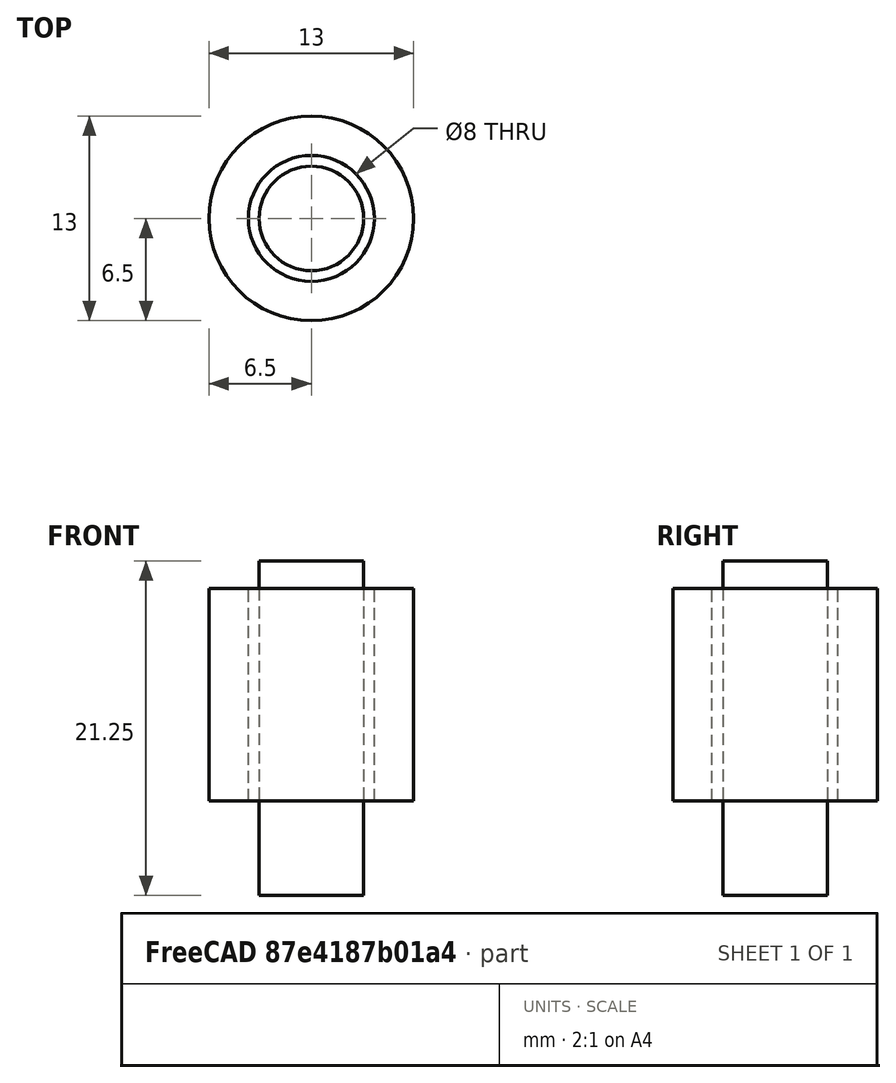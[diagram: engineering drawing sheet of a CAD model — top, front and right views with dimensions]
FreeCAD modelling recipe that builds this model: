
FCSTD DOCUMENT  (FreeCAD 0.18.4R)
Label: shower_handler_vtulka
License: FreeArt
LicenseURL: http://artlibre.org/licence/lal
objects: Part::Cylinder×2, Part::FeaturePython×1, Part::Cut×1
note: 4 computed .brp shape members not serialized (recipe doc carries the construction recipe); baked Part::Feature solids carry a one-line shape summary decoded from their .brp

FEATURE [Part::Cylinder] Cylinder  label="outer cylinder"
  Angle = 360
  AttacherType = Attacher::AttachEngine3D
  Height = 13.5
  Radius = 6.5
FEATURE [Part::FeaturePython] ScrewTap  label="M8x20.0-ScrewTap"  # Fasteners workbench fastener (typed FeaturePython)
  Placement = pos=(0,0,14) rot=(0,0,1;0rad)
  diameter = 9
  invert = false
  length = 20
  matchOuter = false
  offset = 0
  thread = false
FEATURE [Part::Cylinder] Cylinder001  label="inner cylinder"
  Angle = 360
  AttacherType = Attacher::AttachEngine3D
  Height = 13.5
  Radius = 4
FEATURE [Part::Cut] Cut  label="hanger cut"
  Base = -> Cylinder
  Tool = -> Cylinder001
